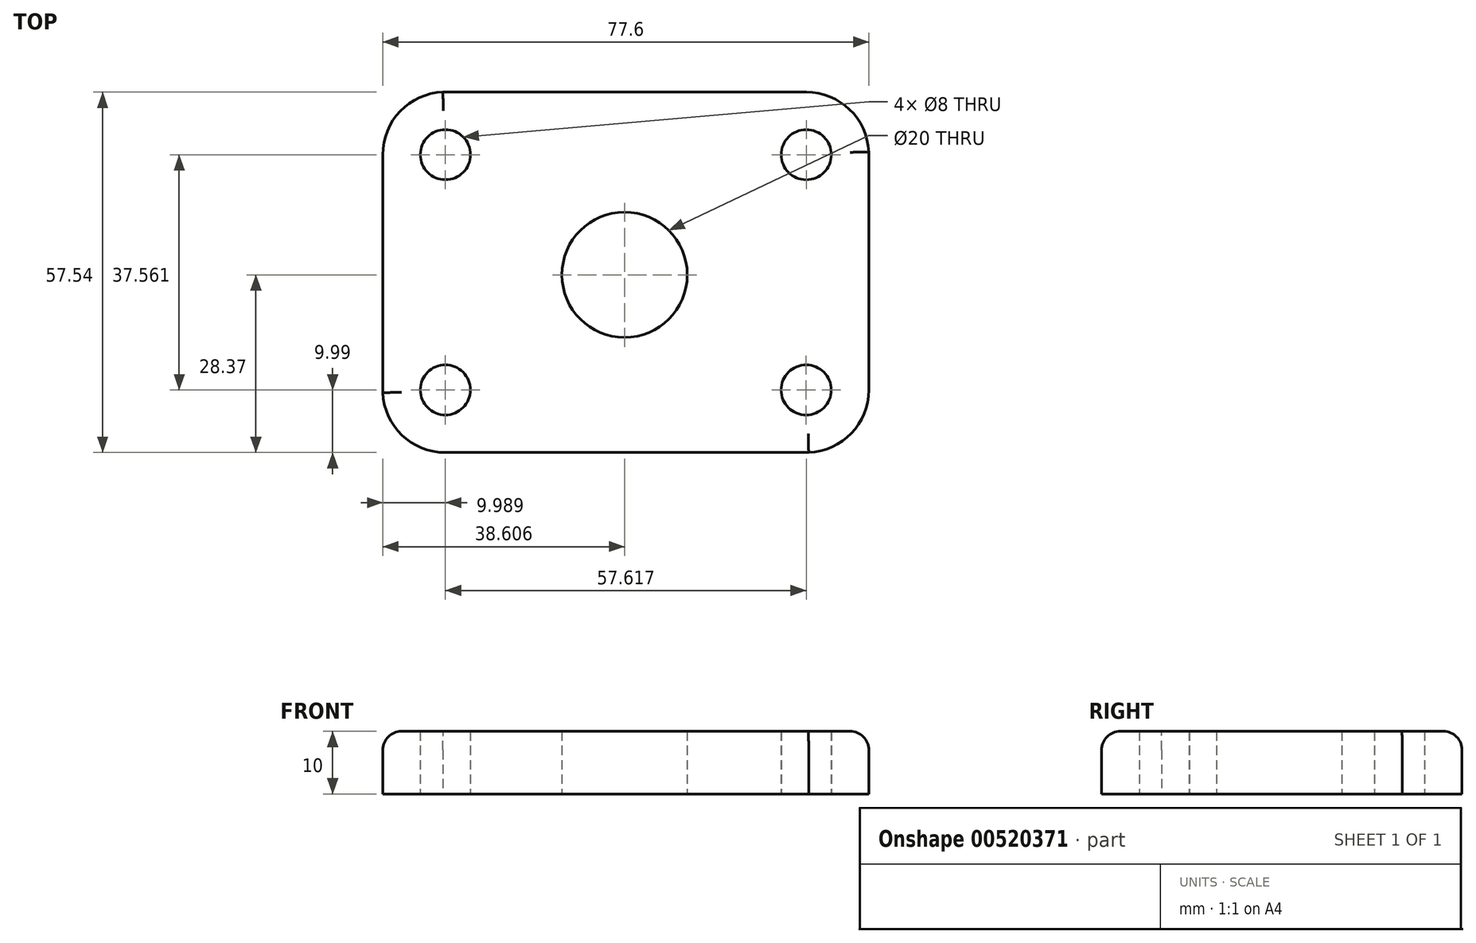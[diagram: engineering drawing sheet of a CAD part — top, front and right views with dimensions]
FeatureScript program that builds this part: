
annotation { "Feature Type Name" : "Feature", "Feature Type Description" : "" }
export const myFeature = defineFeature(function(context is Context, id is Id, definition is map)
    precondition{}
    {
        {
            var Q0;
            Q0=qCreatedBy(makeId("Top.planeOp"),FACE);
            var sketch = newSketch(context, id + "F0", { "sketchPlane" : qUnion([Q0])});
            skLineSegment(sketch, "E0", {"start": v(-40.54, 29.17) * mm, "end": v(17.46, 29.17) * mm});
            skArc(sketch, "E1", {"start": v(27.45, 19.62) * mm, "mid": v(24.37, 26.4) * mm, "end": v(17.46, 29.17) * mm});
            skLineSegment(sketch, "E2", {"start": v(27.45, 19.62) * mm, "end": v(27.45, -18.38) * mm});
            skArc(sketch, "E3", {"start": v(17.84, -28.37) * mm, "mid": v(24.65, -25.31) * mm, "end": v(27.45, -18.38) * mm});
            skLineSegment(sketch, "E4", {"start": v(17.84, -28.37) * mm, "end": v(-40.16, -28.37) * mm});
            skArc(sketch, "E5", {"start": v(-50.15, -18.82) * mm, "mid": v(-47.07, -25.6) * mm, "end": v(-40.16, -28.37) * mm});
            skLineSegment(sketch, "E6", {"start": v(-50.15, -18.82) * mm, "end": v(-50.15, 19.18) * mm});
            skArc(sketch, "E7", {"start": v(-40.54, 29.17) * mm, "mid": v(-47.36, 26.11) * mm, "end": v(-50.15, 19.18) * mm});
            skCircle(sketch, "E8", {"center": v(-11.54, 0) * mm, "radius": 10 * mm});
            skCircle(sketch, "E9", {"center": v(-40.16, -18.37) * mm, "radius": 4 * mm});
            skCircle(sketch, "E10", {"center": v(17.45, -18.38) * mm, "radius": 4 * mm});
            skCircle(sketch, "E11", {"center": v(17.46, 19.17) * mm, "radius": 4 * mm});
            skCircle(sketch, "E12", {"center": v(-40.15, 19.18) * mm, "radius": 4 * mm});
            skLineSegment(sketch, "E13.bottom", {"start": v(26.74, -77.2) * mm, "end": v(-26.74, -77.2) * mm});
            skLineSegment(sketch, "E13.top", {"start": v(26.74, -46.58) * mm, "end": v(-26.74, -46.58) * mm});
            skLineSegment(sketch, "E13.left", {"start": v(36.74, -67.2) * mm, "end": v(36.74, -56.58) * mm});
            skLineSegment(sketch, "E13.right", {"start": v(-36.74, -67.2) * mm, "end": v(-36.74, -56.58) * mm});
            skPoint(sketch, "E13.middle", {"position": v(0, -61.9) * mm});
            skPoint(sketch, "E14.visualSharp", {"position": v(36.74, -46.58) * mm});
            skArc(sketch, "E14.filletArc", {"start": v(36.74, -56.58) * mm, "mid": v(33.81, -49.51) * mm, "end": v(26.74, -46.58) * mm});
            skPoint(sketch, "E15.visualSharp", {"position": v(-36.74, -46.58) * mm});
            skArc(sketch, "E15.filletArc", {"start": v(-26.74, -46.58) * mm, "mid": v(-33.81, -49.51) * mm, "end": v(-36.74, -56.58) * mm});
            skPoint(sketch, "E16.visualSharp", {"position": v(-36.74, -77.2) * mm});
            skArc(sketch, "E16.filletArc", {"start": v(-36.74, -67.2) * mm, "mid": v(-33.81, -74.28) * mm, "end": v(-26.74, -77.2) * mm});
            skPoint(sketch, "E17.visualSharp", {"position": v(36.74, -77.2) * mm});
            skArc(sketch, "E17.filletArc", {"start": v(26.74, -77.2) * mm, "mid": v(33.81, -74.28) * mm, "end": v(36.74, -67.2) * mm});
            skSolve(sketch);
        }
        {
            var Q0;
            Q0=makeQuery(id+"F0.imprint","IMPRINT",FACE,{"disambiguationData":[TD([[makeQuery(id+"F0.imprint","IMPRINT",EDGE,{"derivedFrom":sQuery(id+"F0.wireOp",EDGE,"E0")}),-1.0]])]});
            extrude(context, id + "F1", {"entities" : qUnion([Q0]), "depth" : 10 * mm, "offsetDistance" : 25 * mm});
        }
        {
            var Q0;
            Q0=makeQuery(id+"F1.opExtrude","CAP_EDGE",EDGE,{"disambiguationData":[OSD([sQuery(id+"F0.wireOp",EDGE,"E6")])],"isStart":false});
            var Q1;
            Q1=makeQuery(id+"F1.opExtrude","CAP_EDGE",EDGE,{"disambiguationData":[OSD([sQuery(id+"F0.wireOp",EDGE,"E5")])],"isStart":false});
            var Q2;
            Q2=makeQuery(id+"F1.opExtrude","CAP_EDGE",EDGE,{"disambiguationData":[OSD([sQuery(id+"F0.wireOp",EDGE,"E4")])],"isStart":false});
            var Q3;
            Q3=makeQuery(id+"F1.opExtrude","CAP_EDGE",EDGE,{"disambiguationData":[OSD([sQuery(id+"F0.wireOp",EDGE,"E3")])],"isStart":false});
            var Q4;
            Q4=makeQuery(id+"F1.opExtrude","CAP_EDGE",EDGE,{"disambiguationData":[OSD([sQuery(id+"F0.wireOp",EDGE,"E2")])],"isStart":false});
            var Q5;
            Q5=makeQuery(id+"F1.opExtrude","CAP_EDGE",EDGE,{"disambiguationData":[OSD([sQuery(id+"F0.wireOp",EDGE,"E1")])],"isStart":false});
            var Q6;
            Q6=makeQuery(id+"F1.opExtrude","CAP_EDGE",EDGE,{"disambiguationData":[OSD([sQuery(id+"F0.wireOp",EDGE,"E0")])],"isStart":false});
            fillet(context, id + "F2", {"entities" : qUnion([Q0, Q1, Q2, Q3, Q4, Q5, Q6]), "radius" : 3 * mm, "tangentPropagation" : true, "allowEdgeOverflow" : false});
        }
    });
